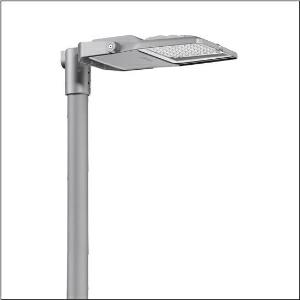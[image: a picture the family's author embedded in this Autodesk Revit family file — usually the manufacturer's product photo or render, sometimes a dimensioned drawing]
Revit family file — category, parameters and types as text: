
# Revit family: floodlight_fl_21_iq_mini___pl43_5xa7771d4a3a_2bc1
name_source: partatom
category: Lighting Fixtures
units: mm (PartAtom-declared; Revit-internal decimal feet)

## family parameters
Cut with Voids When Loaded = No
Host = Face
Light Source = No
Part Type = Normal
Room Calculation Point = No
Round Connector Dimension = Use Diameter
Shared = No

## types (1)
- --- (1 x LED, 19090 lm, 143 W, 4000K)
    Apparent Load = 143 VA
    CIE Flux Codes = 27 78 99 100 100
    Color Rendering = 70
    Color Temperature = 4000K
    Default Elevation = 1800 mm
    Description = Floodlight FL 21 iQ mini, floodlight, primary light control with lens, of PMMA, primary optical cover: protective disc, of toughened safety glass, transparent, light distribution: PL43, light emission: direct distribution, installation type: surface-mounted, lamps: LED, High Power LED, rated values: 19.090lm | 143W | 133,5lm/W (begin service life); end service life: 19.090lm | 151,6W; at 50% lumin. flux: 9.545lm | 60,8W | 157lm/W, colour temperature: 4000K, colour rendering: CRI > 70, light colour: 740, light setting 1 begin service life: 100% | 19.090lm | 143W | 133,5lm/W | 4.000K, light setting 1 end service life: 151,6W, further light settings possible, control: Auto-Match, Temp-Guard, Lumen-Switch, Night-Set, Smart-Wire, Light-Fading, Desk-Remote (wireless, voltage-free reading and setting of iQ features in the workshop via application-optimized NFC function/RFID function), optimised constant luminous flux control (CLO 2.0), pre-setting: linear dimming characteristic, with terminal, 6-pole, mains connection: 220..240V, AC, 50/60Hz, luminaire housing, of diecast aluminium, powder-coated, SITECO metallic grey (DB 702S), corrosivity category C5 mid according to DIN EN ISO 12944suitable for swimming poolschlorine-resistant, sealing non-destructively replaceable, please order mast flange separately, mast bracket, of steel, galvanised, powder-coated, SITECO metallic grey (DB 702S), protection rating (complete): IP66, insulation class (complete): insulation class II (safety insulation), certification: CE, ENEC, VDE, protection symbol: D, impact resistance: IK08, permissible operating ambient temperature: -40..+40°C, permissible operating ambient temperature for outdoor applications: -40..+50°C, standard: DIN EN 12944, LABS conformity tested according to VDMA 24364:2018-05, packaging unit: 1 piece

Light Distribution: PL43
    Height = 70 mm
    Lamp = 1 x LED
    Lamp Light Flux = 19090 lm
    Lamp Power = 143 W
    Lamp count = 1
    Length = 485 mm
    Luminous efficacy = 133 lm/W
    Manufacturer = Siteco
    ModVariant = No
    Model = 5XA7771D4A3A
    Mounting Place = Pole
    Mounting Type = Pole annexe
    Number of Poles = 1
    OnlyDefault = Yes
    Power Factor = 1
    Product Name = Floodlight FL 21 iQ mini | PL43
    Product group = floodlight | pylon annexe
    ProductGroupID = 6201
    Protection Class = Protection class II
    Protection Degree = IP 66
    RLX_Detail_Level = 1
    RLX_Emergency_Light_Flux = 0 lm
    RLX_Emergency_Type = 0
    RLX_Emergency_Type_DB = No
    RlxData = <blob elided: 101841 chars, md5=d84bcd08>
    Socket = socket
    Standby Power = 0 W
    System Light Flux = 19090 lm
    System Power = 143 W
    Type Comments = factory setting: luminous flux: 100 % | dim-lin: 254 | 730 mA
    Type Image = l_1007125.jpg
    URL = http://relux.com
    VarID = @adj_162771
    Voltage = 0 V
    Weight = 0.00 kg
    Width = 337 mm

## geometry (parser evidence)
native form markers: Blend x4, Sweep x13
no freeform markers — native parametric forms only
